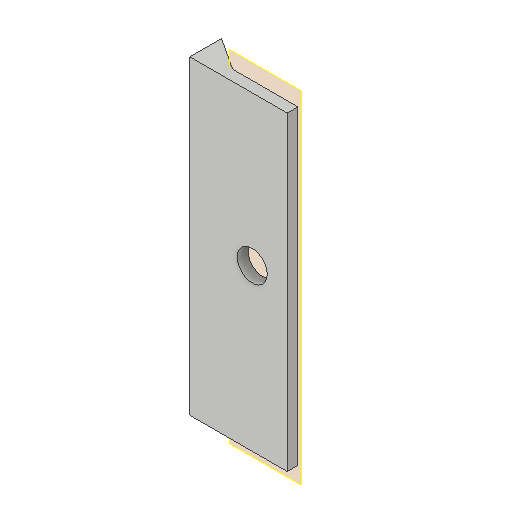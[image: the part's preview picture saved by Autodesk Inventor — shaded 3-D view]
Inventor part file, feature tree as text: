
AUTODESK INVENTOR PART (.ipt)
format: ipt  version: 2022 (Build 260153000, 153)  size: 100,864 bytes
history: native  units: mm
features: other x3, extrude x2, sketch x2, reference x2, plane x1, projected_geometry x1
ambient origin geometry x8: Origin, YZ Plane, XZ Plane, XY Plane, X Axis, Y Axis, Z Axis, Center Point
bodies: Solid1 (feature_tree)
feature tree (11):
  plane  "Work Plane1"
  extrude  "Extrusion1"  Depth=1.0mm TaperAngle=0.0deg
  extrude  "Extrusion2"  [1 undecoded]
  sketch  "Sketch1"  dims[d0=3.0mm d1=1.0mm d2=0.0mm]
  reference  "Reference1"
  reference  "Reference2"
  sketch  "Sketch2"  dims[d3=1.0mm d4=0.0mm]
  projected_geometry  "Projected Loop1"
  other  "<userpath>\Documents\GitHub\cellstorm\INVENTOR\cellSTORM_v6.iam"
  other  "cellSTORM_v6.iam"
  other  "cellSTORM_v5_chiptray_old_0:1"
note: 1 required parameter value undecoded (feature->parameter linkage not recoverable at this tier; creation-order binding heuristic only, values carry confidence <= 0.55)
